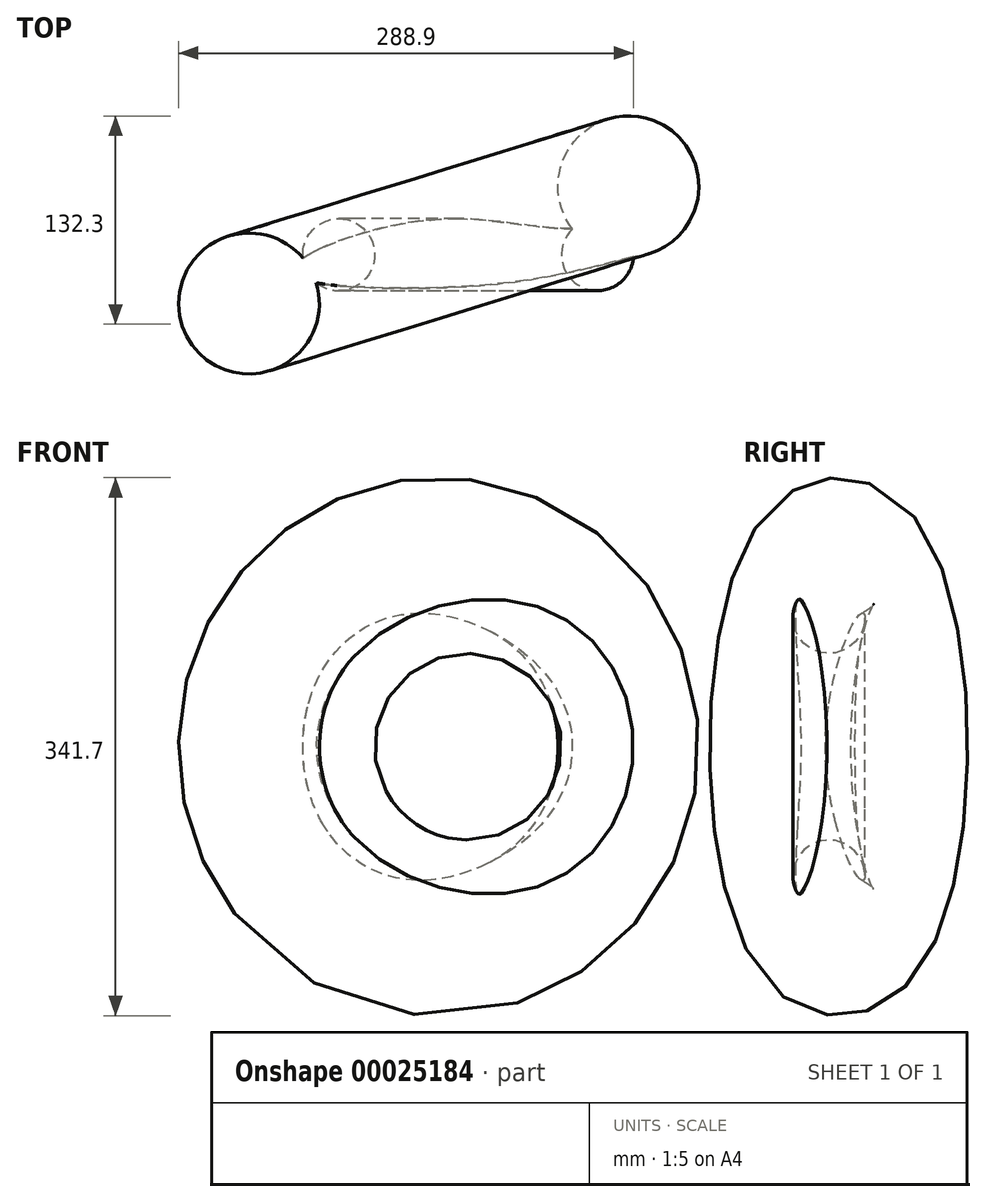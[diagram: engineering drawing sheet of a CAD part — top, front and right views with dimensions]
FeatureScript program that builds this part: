
annotation { "Feature Type Name" : "Feature", "Feature Type Description" : "" }
export const myFeature = defineFeature(function(context is Context, id is Id, definition is map)
    precondition{}
    {
        {
            var Q0;
            Q0=qCreatedBy(makeId("Top.planeOp"),FACE);
            var sketch = newSketch(context, id + "F0", { "sketchPlane" : qUnion([Q0])});
            skCircle(sketch, "E0", {"center": v(38.13, 0) * mm, "radius": 22.84 * mm});
            skLineSegment(sketch, "E1", {"start": v(-44.03, 12.6) * mm, "end": v(-44.03, -19.18) * mm});
            skSolve(sketch);
        }
        {
            var Q0;
            Q0=makeQuery(id+"F0.imprint","IMPRINT",FACE,{"disambiguationData":[TD([[makeQuery(id+"F0.imprint","IMPRINT",EDGE,{"derivedFrom":sQuery(id+"F0.wireOp",EDGE,"E0")}),1.0]])]});
            var Q1;
            Q1=sQuery(id+"F0.wireOp",EDGE,"E1");
            revolve(context, id + "F1", {"entities" : qUnion([Q0]), "axis" : qUnion([Q1]), "revolveType" : RevolveType.FULL});
        }
        {
            var Q0;
            Q0=qCreatedBy(makeId("Top.planeOp"),FACE);
            var sketch = newSketch(context, id + "F2", { "sketchPlane" : qUnion([Q0])});
            skCircle(sketch, "E2", {"center": v(57.79, 43.4) * mm, "radius": 44.73 * mm});
            skLineSegment(sketch, "E3", {"start": v(-53.97, -22.16) * mm, "end": v(-69.59, 28.45) * mm});
            skSolve(sketch);
        }
        {
            var Q0;
            Q0=makeQuery(id+"F2.imprint","IMPRINT",FACE,{"disambiguationData":[TD([[makeQuery(id+"F2.imprint","IMPRINT",EDGE,{"derivedFrom":sQuery(id+"F2.wireOp",EDGE,"E2")}),1.0]])]});
            var Q1;
            Q1=sQuery(id+"F2.wireOp",EDGE,"E3");
            revolve(context, id + "F3", {"operationType" : NewBodyOperationType.ADD, "entities" : qUnion([Q0]), "axis" : qUnion([Q1]), "revolveType" : RevolveType.FULL});
        }
    });
